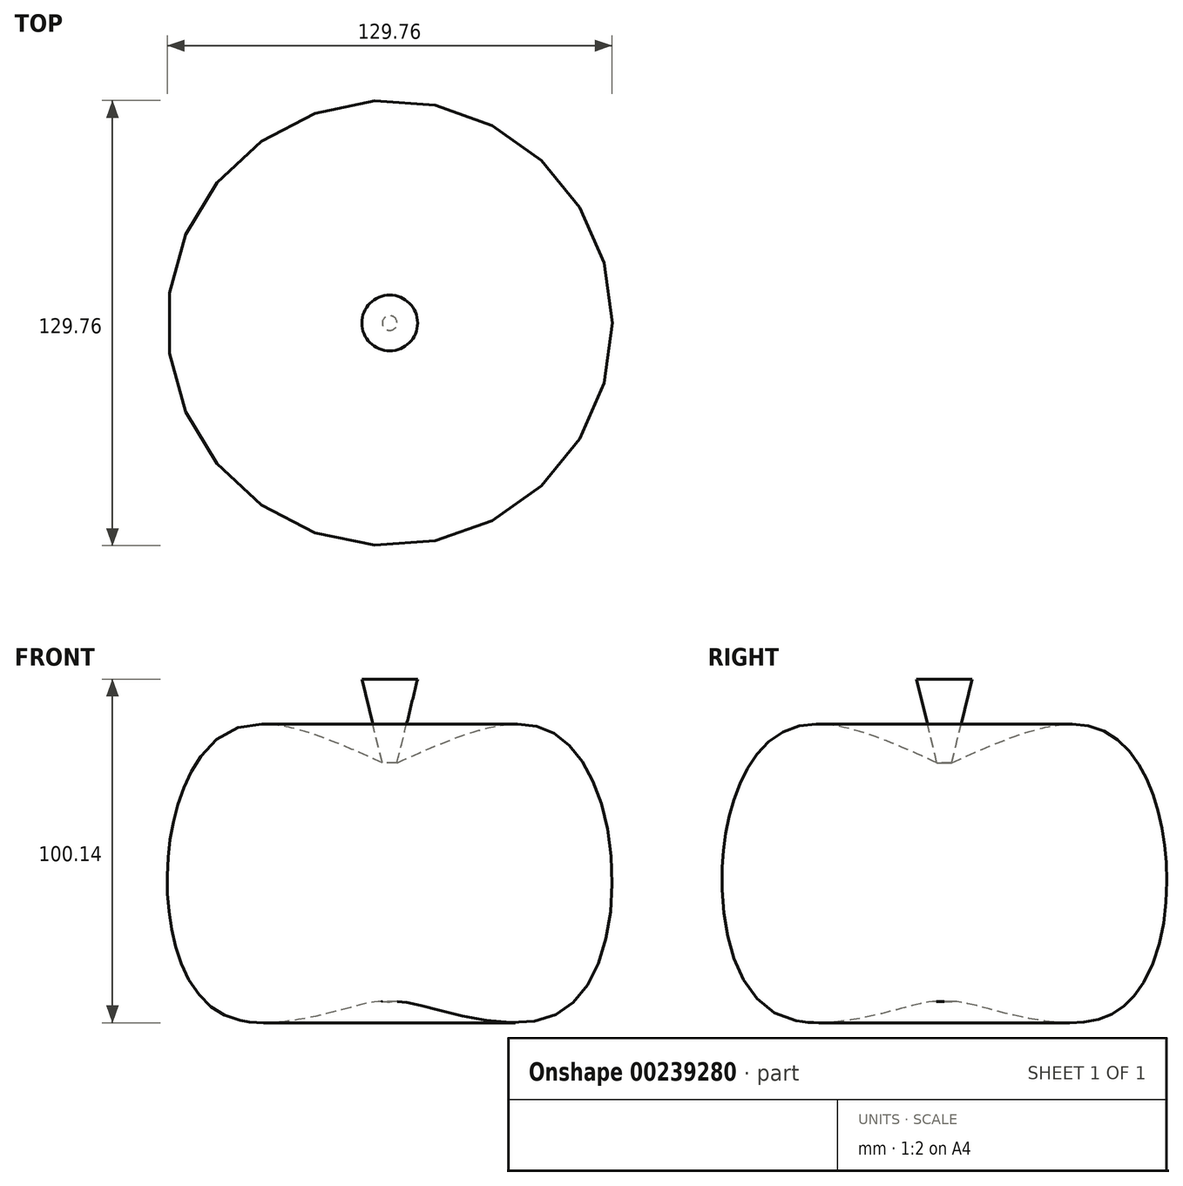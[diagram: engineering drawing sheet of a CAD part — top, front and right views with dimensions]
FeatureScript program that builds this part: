
annotation { "Feature Type Name" : "Feature", "Feature Type Description" : "" }
export const myFeature = defineFeature(function(context is Context, id is Id, definition is map)
    precondition{}
    {
        {
            var Q0;
            Q0=qCreatedBy(makeId("Front.planeOp"),FACE);
            var sketch = newSketch(context, id + "F0", { "sketchPlane" : qUnion([Q0])});
            skLineSegment(sketch, "E0", {"start": v(0, 30.8) * mm, "end": v(8.12, 30.8) * mm});
            skLineSegment(sketch, "E1", {"start": v(8.12, 30.8) * mm, "end": v(2.15, 6.44) * mm});
            skFitSpline(sketch, "E2", {"points": [v(2.15, 6.44) * mm, v(45.06, 16.4) * mm, v(64.53, -20.23) * mm, v(47.82, -67.29) * mm, v(6.28, -63.6) * mm, v(0, -63.3) * mm], "startDerivative": vector(207.62, 94.13) * mm, "endDerivative": vector(-52.06, -6.55) * mm});
            skLineSegment(sketch, "E3", {"start": v(0, 30.8) * mm, "end": v(0, -63.3) * mm});
            skSolve(sketch);
        }
        {
            var Q0;
            Q0=qSketchRegion(id+"F0",true);
            var Q1;
            Q1=sQuery(id+"F0.wireOp",EDGE,"E3");
            revolve(context, id + "F1", {"entities" : qUnion([Q0]), "axis" : qUnion([Q1]), "revolveType" : RevolveType.FULL});
        }
    });
